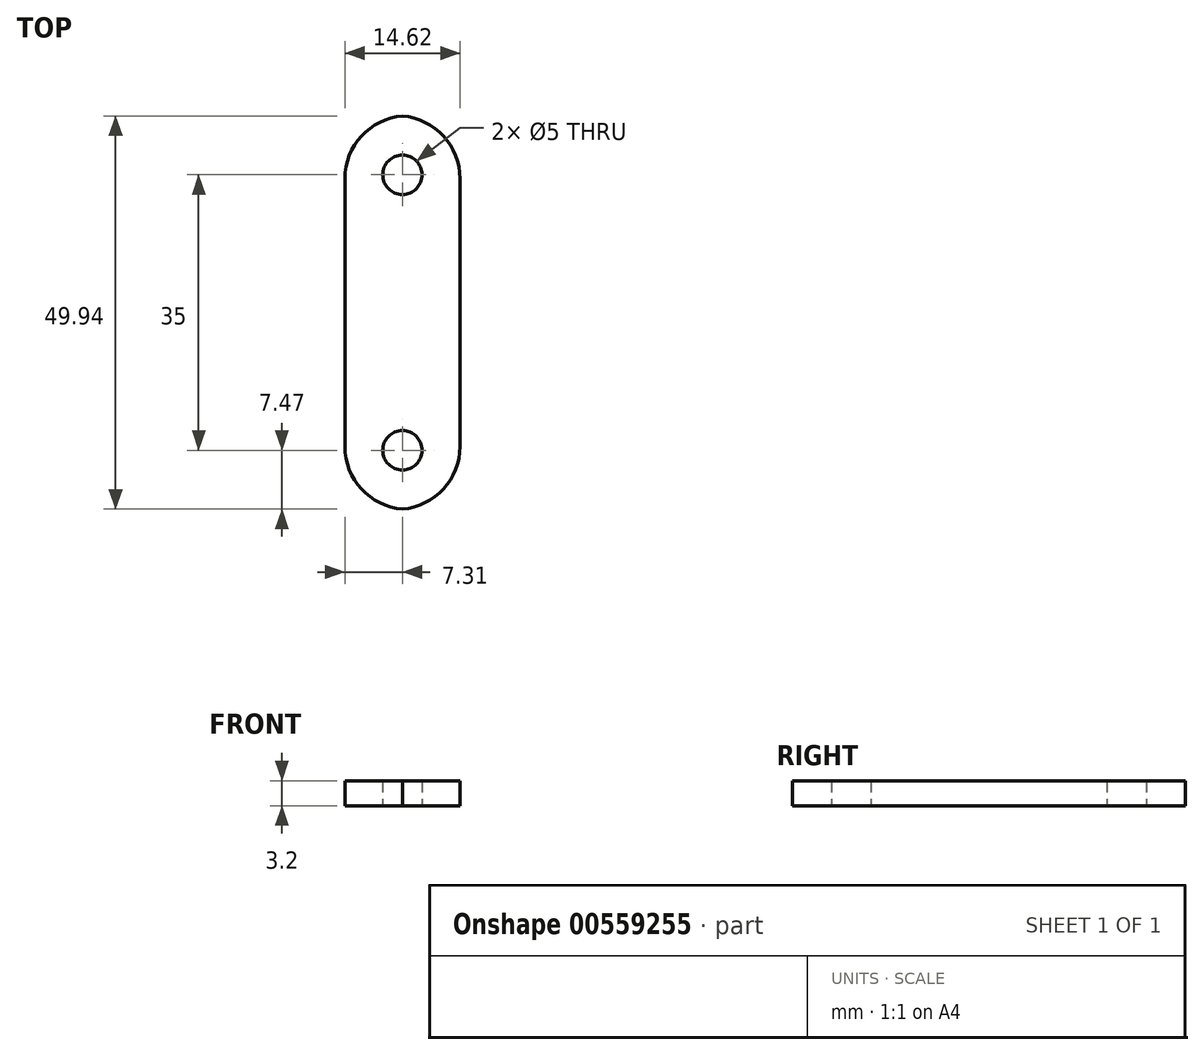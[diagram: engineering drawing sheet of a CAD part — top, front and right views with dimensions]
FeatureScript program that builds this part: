
annotation { "Feature Type Name" : "Feature", "Feature Type Description" : "" }
export const myFeature = defineFeature(function(context is Context, id is Id, definition is map)
    precondition{}
    {
        {
            var Q0;
            Q0=qCreatedBy(makeId("Top.planeOp"),FACE);
            var sketch = newSketch(context, id + "F0", { "sketchPlane" : qUnion([Q0])});
            skLineSegment(sketch, "E0.bottom", {"start": v(7.3, -25) * mm, "end": v(-7.3, -25) * mm});
            skLineSegment(sketch, "E0.top", {"start": v(7.3, 25) * mm, "end": v(-7.3, 25) * mm});
            skLineSegment(sketch, "E0.left", {"start": v(7.3, -25) * mm, "end": v(7.3, 25) * mm});
            skLineSegment(sketch, "E0.right", {"start": v(-7.3, -25) * mm, "end": v(-7.3, 25) * mm});
            skPoint(sketch, "E0.middle", {"position": v(0, 0) * mm});
            skCircle(sketch, "E1", {"center": v(0, 17.5) * mm, "radius": 2.5 * mm});
            skCircle(sketch, "E2", {"center": v(0, -17.5) * mm, "radius": 2.5 * mm});
            skSolve(sketch);
        }
        {
            var Q0;
            Q0=qSketchRegion(id+"F0",true);
            extrude(context, id + "F1", {"entities" : qUnion([Q0]), "depth" : 3.2 * mm});
        }
        {
            var Q0;
            Q0=makeQuery(id+"F1.opExtrude","SWEPT_EDGE",EDGE,{"disambiguationData":[OSD([sQuery(id+"F0.wireOp",EDGE,"E0.bottom"),sQuery(id+"F0.wireOp",EDGE,"E0.left")])]});
            var Q1;
            Q1=makeQuery(id+"F1.opExtrude","SWEPT_EDGE",EDGE,{"disambiguationData":[OSD([sQuery(id+"F0.wireOp",EDGE,"E0.bottom"),sQuery(id+"F0.wireOp",EDGE,"E0.right")])]});
            fillet(context, id + "F2", {"entities" : qUnion([Q0, Q1]), "radius" : 8 * mm, "tangentPropagation" : true, "allowEdgeOverflow" : false});
        }
        {
            var Q0;
            Q0=makeQuery(id+"F1.opExtrude","SWEPT_EDGE",EDGE,{"disambiguationData":[OSD([sQuery(id+"F0.wireOp",EDGE,"E0.top"),sQuery(id+"F0.wireOp",EDGE,"E0.left")])]});
            var Q1;
            Q1=makeQuery(id+"F1.opExtrude","SWEPT_EDGE",EDGE,{"disambiguationData":[OSD([sQuery(id+"F0.wireOp",EDGE,"E0.top"),sQuery(id+"F0.wireOp",EDGE,"E0.right")])]});
            fillet(context, id + "F3", {"entities" : qUnion([Q0, Q1]), "radius" : 8 * mm, "tangentPropagation" : true, "allowEdgeOverflow" : false});
        }
    });
